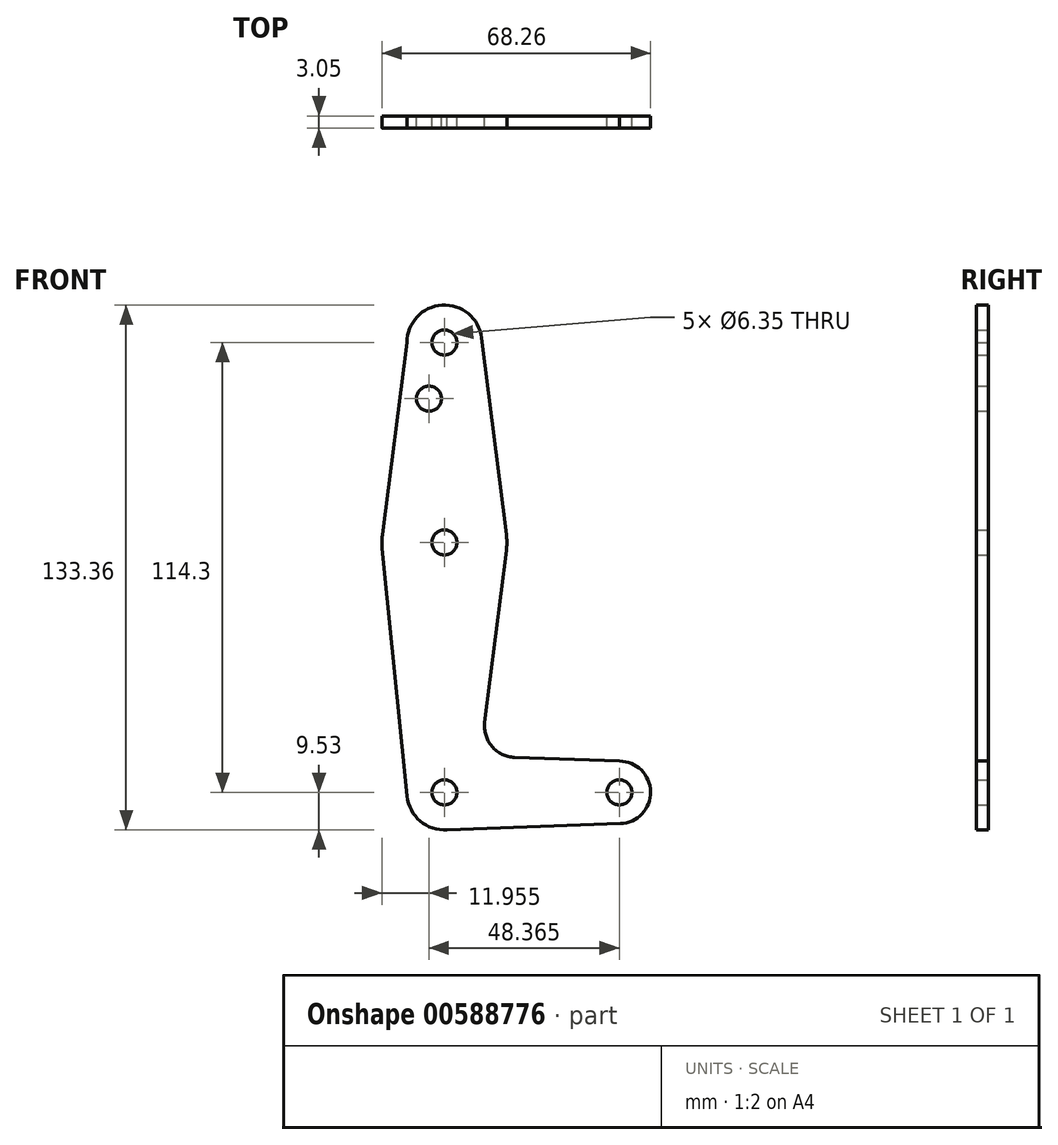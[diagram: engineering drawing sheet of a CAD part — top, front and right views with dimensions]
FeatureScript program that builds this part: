
annotation { "Feature Type Name" : "Feature", "Feature Type Description" : "" }
export const myFeature = defineFeature(function(context is Context, id is Id, definition is map)
    precondition{}
    {
        {
            var Q0;
            Q0=qCreatedBy(makeId("Front.planeOp"),FACE);
            var sketch = newSketch(context, id + "F0", { "sketchPlane" : qUnion([Q0])});
            skCircle(sketch, "E0", {"center": v(0, 114.3) * mm, "radius": 9.52 * mm});
            skCircle(sketch, "E1", {"center": v(0, 0) * mm, "radius": 9.53 * mm});
            skCircle(sketch, "E2", {"center": v(0, 63.5) * mm, "radius": 15.88 * mm});
            skCircle(sketch, "E3", {"center": v(44.45, 0) * mm, "radius": 7.94 * mm});
            skLineSegment(sketch, "E4", {"start": v(0, 114.3) * mm, "end": v(0, 0) * mm, "construction": true});
            skLineSegment(sketch, "E5", {"start": v(44.45, 0) * mm, "end": v(0, 0) * mm, "construction": true});
            skLineSegment(sketch, "E6", {"start": v(-9.53, 114.3) * mm, "end": v(-15.75, 65.5) * mm});
            skLineSegment(sketch, "E7", {"start": v(0, -9.52) * mm, "end": v(44.73, -7.93) * mm});
            skLineSegment(sketch, "E8", {"start": v(15.75, 65.48) * mm, "end": v(9.45, 115.5) * mm});
            skCircle(sketch, "E9", {"center": v(0, 114.3) * mm, "radius": 3.18 * mm});
            skCircle(sketch, "E10", {"center": v(0, 63.5) * mm, "radius": 3.18 * mm});
            skCircle(sketch, "E11", {"center": v(0, 0) * mm, "radius": 3.18 * mm});
            skCircle(sketch, "E12", {"center": v(44.45, 0) * mm, "radius": 3.17 * mm});
            skCircle(sketch, "E13", {"center": v(-3.91, 100.03) * mm, "radius": 3.18 * mm});
            skPoint(sketch, "E14.newPointA", {"position": v(9.57, 0) * mm});
            skLineSegment(sketch, "E15", {"start": v(44.45, 7.94) * mm, "end": v(17.85, 8.9) * mm});
            skLineSegment(sketch, "E16", {"start": v(15.75, 61.52) * mm, "end": v(10.25, 17.83) * mm});
            skArc(sketch, "E17.filletArc", {"start": v(10.25, 17.83) * mm, "mid": v(12.08, 11.69) * mm, "end": v(17.85, 8.9) * mm});
            skPoint(sketch, "E18.end.orphan", {"position": v(-9.57, 0) * mm});
            skLineSegment(sketch, "E19", {"start": v(-9.48, -0.95) * mm, "end": v(-15.8, 61.91) * mm});
            skSolve(sketch);
        }
        {
            var Q0;
            Q0 = qSketchRegion(id + "F0", true);
            extrude(context, id + "F1", {"entities" : qUnion([Q0]), "depth" : 3.05 * mm, "offsetDistance" : 25.4 * mm});
        }
    });
